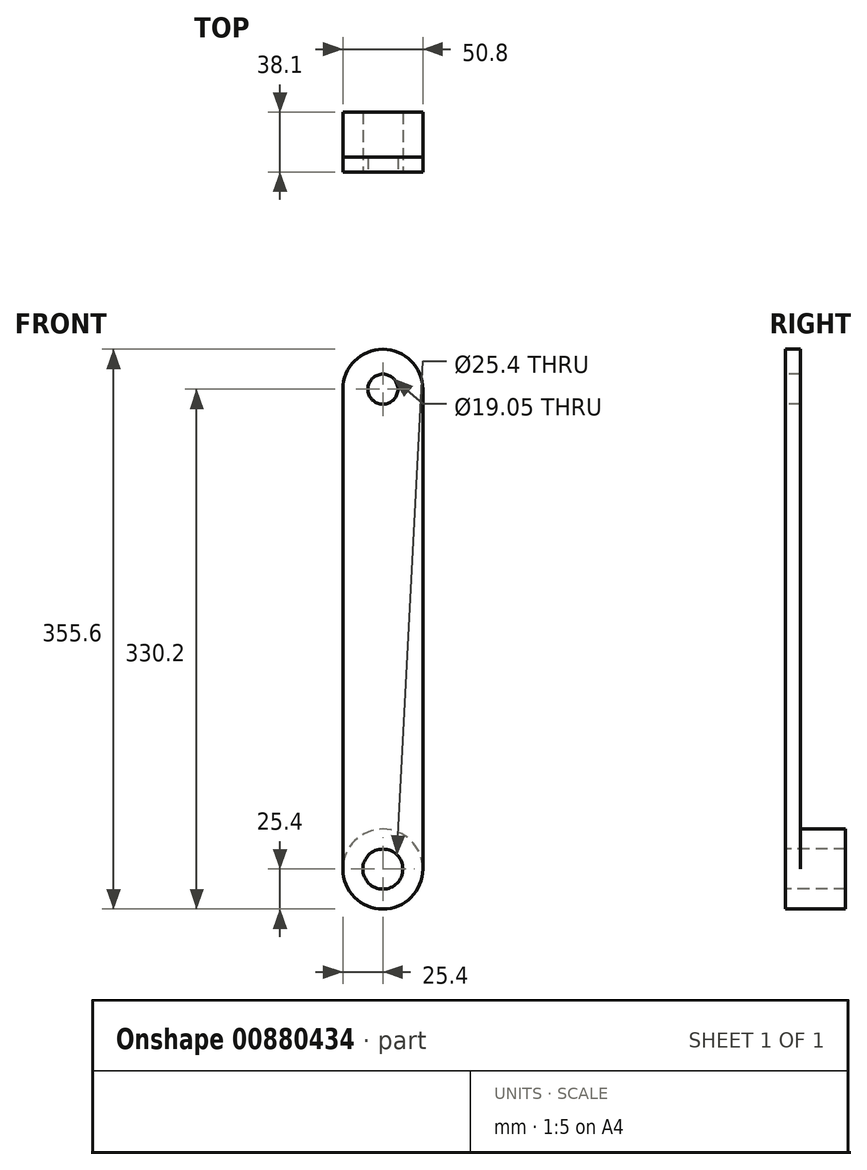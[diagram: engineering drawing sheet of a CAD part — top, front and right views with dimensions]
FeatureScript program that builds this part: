
annotation { "Feature Type Name" : "Feature", "Feature Type Description" : "" }
export const myFeature = defineFeature(function(context is Context, id is Id, definition is map)
    precondition{}
    {
        {
            var Q0;
            Q0=qCreatedBy(makeId("Front.planeOp"),FACE);
            var sketch = newSketch(context, id + "F0", { "sketchPlane" : qUnion([Q0])});
            skCircle(sketch, "E0", {"center": v(0, 0) * mm, "radius": 25.4 * mm});
            skCircle(sketch, "E1", {"center": v(0, 0) * mm, "radius": 12.7 * mm});
            skSolve(sketch);
        }
        {
            var Q0;
            Q0=makeQuery(id+"F0.imprint","IMPRINT",FACE,{"disambiguationData":[TD([[makeQuery(id+"F0.imprint","IMPRINT",EDGE,{"derivedFrom":sQuery(id+"F0.wireOp",EDGE,"E0")}),1.0]])]});
            extrude(context, id + "F1", {"entities" : qUnion([Q0]), "oppositeDirection" : true, "depth" : 38.1 * mm, "offsetDistance" : 25.4 * mm});
        }
        {
            var Q0;
            Q0=qCreatedBy(makeId("Front.planeOp"),FACE);
            var sketch = newSketch(context, id + "F2", { "sketchPlane" : qUnion([Q0])});
            skLineSegment(sketch, "E2.bottom", {"start": v(-25.4, 0) * mm, "end": v(25.4, 0) * mm});
            skLineSegment(sketch, "E2.top", {"start": v(-25.4, 304.8) * mm, "end": v(25.4, 304.8) * mm});
            skLineSegment(sketch, "E2.left", {"start": v(-25.4, 0) * mm, "end": v(-25.4, 304.8) * mm});
            skLineSegment(sketch, "E2.right", {"start": v(25.4, 0) * mm, "end": v(25.4, 304.8) * mm});
            skArc(sketch, "E3", {"start": v(25.4, 304.8) * mm, "mid": v(0, 330.2) * mm, "end": v(-25.4, 304.8) * mm});
            skCircle(sketch, "E4", {"center": v(0, 304.8) * mm, "radius": 9.53 * mm});
            skCircle(sketch, "E5", {"center": v(0, 0) * mm, "radius": 12.7 * mm});
            skSolve(sketch);
        }
        {
            var Q0;
            {var subQ1=sQuery(id+"F2.wireOp",EDGE,"E2.left");Q0=makeQuery(id+"F2.imprint","IMPRINT",FACE,{"disambiguationData":[TD([[makeQuery(id+"F2.imprint","IMPRINT",EDGE,{"derivedFrom":subQ1}),-1.0]])]});}
            var Q1;
            {var subQ0=sQuery(id+"F2.wireOp",EDGE,"E3");Q1=makeQuery(id+"F2.imprint","IMPRINT",FACE,{"disambiguationData":[TD([[makeQuery(id+"F2.imprint","IMPRINT",EDGE,{"derivedFrom":subQ0}),1.0]])]});}
            extrude(context, id + "F3", {"entities" : qUnion([Q0, Q1]), "operationType" : NewBodyOperationType.ADD, "oppositeDirection" : true, "depth" : 9.52 * mm, "offsetDistance" : 25.4 * mm});
        }
    });
